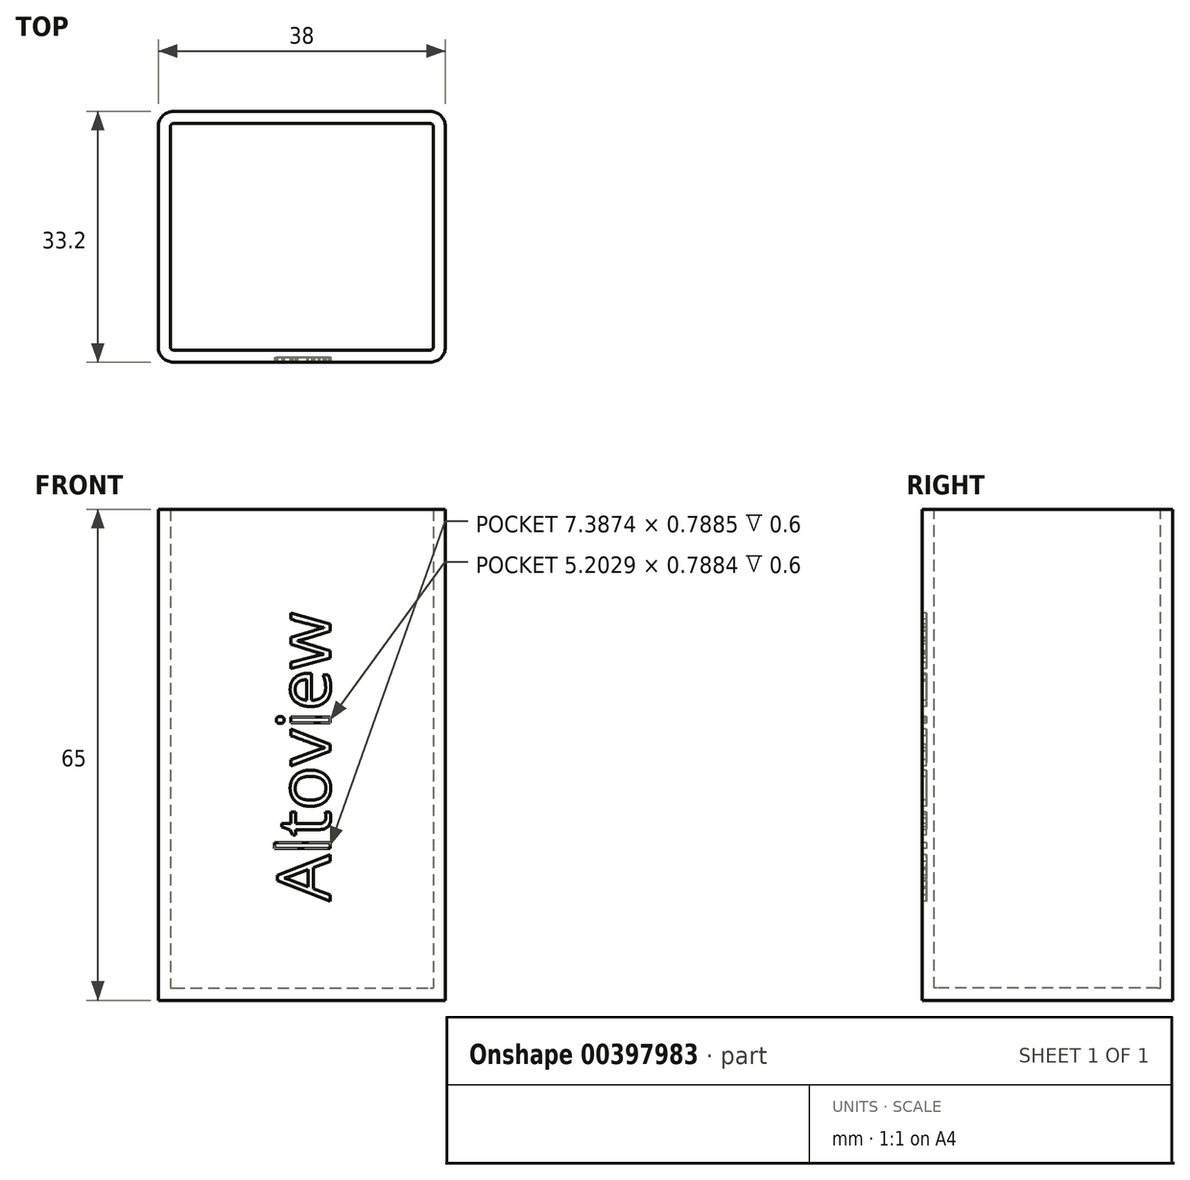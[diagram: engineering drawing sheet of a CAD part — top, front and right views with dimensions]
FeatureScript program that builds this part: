
annotation { "Feature Type Name" : "Feature", "Feature Type Description" : "" }
export const myFeature = defineFeature(function(context is Context, id is Id, definition is map)
    precondition{}
    {
        {
            var Q0;
            Q0=qCreatedBy(makeId("Top.planeOp"),FACE);
            var sketch = newSketch(context, id + "F0", { "sketchPlane" : qUnion([Q0])});
            skLineSegment(sketch, "E0.bottom", {"start": v(-17, 16.6) * mm, "end": v(17, 16.6) * mm});
            skLineSegment(sketch, "E0.top", {"start": v(-17, -16.6) * mm, "end": v(17, -16.6) * mm});
            skLineSegment(sketch, "E0.left", {"start": v(-19, 14.6) * mm, "end": v(-19, -14.6) * mm});
            skLineSegment(sketch, "E0.right", {"start": v(19, 14.6) * mm, "end": v(19, -14.6) * mm});
            skPoint(sketch, "E1.visualSharp", {"position": v(-19, 16.6) * mm});
            skArc(sketch, "E1.filletArc", {"start": v(-17, 16.6) * mm, "mid": v(-18.41, 16.01) * mm, "end": v(-19, 14.6) * mm});
            skPoint(sketch, "E2.visualSharp", {"position": v(-19, -16.6) * mm});
            skArc(sketch, "E2.filletArc", {"start": v(-19, -14.6) * mm, "mid": v(-18.41, -16.01) * mm, "end": v(-17, -16.6) * mm});
            skPoint(sketch, "E3.visualSharp", {"position": v(19, -16.6) * mm});
            skArc(sketch, "E3.filletArc", {"start": v(17, -16.6) * mm, "mid": v(18.41, -16.01) * mm, "end": v(19, -14.6) * mm});
            skPoint(sketch, "E4.visualSharp", {"position": v(19, 16.6) * mm});
            skArc(sketch, "E4.filletArc", {"start": v(19, 14.6) * mm, "mid": v(18.41, 16.01) * mm, "end": v(17, 16.6) * mm});
            skSolve(sketch);
        }
        {
            var Q0;
            Q0=makeQuery(id+"F0.imprint","IMPRINT",FACE,{"disambiguationData":[TD([[makeQuery(id+"F0.imprint","IMPRINT",EDGE,{"derivedFrom":sQuery(id+"F0.wireOp",EDGE,"E0.bottom")}),-1.0]])]});
            extrude(context, id + "F1", {"entities" : qUnion([Q0]), "depth" : 65 * mm});
        }
        {
            var Q0;
            Q0=makeQuery(id+"F1.opExtrude","CAP_FACE",FACE,{"disambiguationData":[OSD([sQuery(id+"F0.wireOp",EDGE,"E0.bottom"),sQuery(id+"F0.wireOp",EDGE,"E0.top"),sQuery(id+"F0.wireOp",EDGE,"E0.left"),sQuery(id+"F0.wireOp",EDGE,"E0.right")])],"isStart":false});
            shell(context, id + "F2", {"entities" : qUnion([Q0]), "thickness" : 1.6 * mm});
        }
        {
            var Q0;
            Q0=makeQuery(id+"F1.opExtrude","SWEPT_FACE",FACE,{"disambiguationData":[OSD([sQuery(id+"F0.wireOp",EDGE,"E0.top")])]});
            var sketch = newSketch(context, id + "F3", { "sketchPlane" : qUnion([Q0])});
            skText(sketch, "E5", { "text": "Altoview", "fontName": "OpenSans-Regular.ttf"});
            const initialGuessF3  = {"E5": [0.00375, 0.0131, 0, 1, 0.007]};
            skSetInitialGuess(sketch, initialGuessF3);
            skSolve(sketch);
        }
        {
            var Q0;
            Q0 = qSketchRegion(id + "F3", true);
            extrude(context, id + "F4", {"entities" : qUnion([Q0]), "operationType" : NewBodyOperationType.REMOVE, "oppositeDirection" : true, "depth" : .6 * mm});
        }
    });
